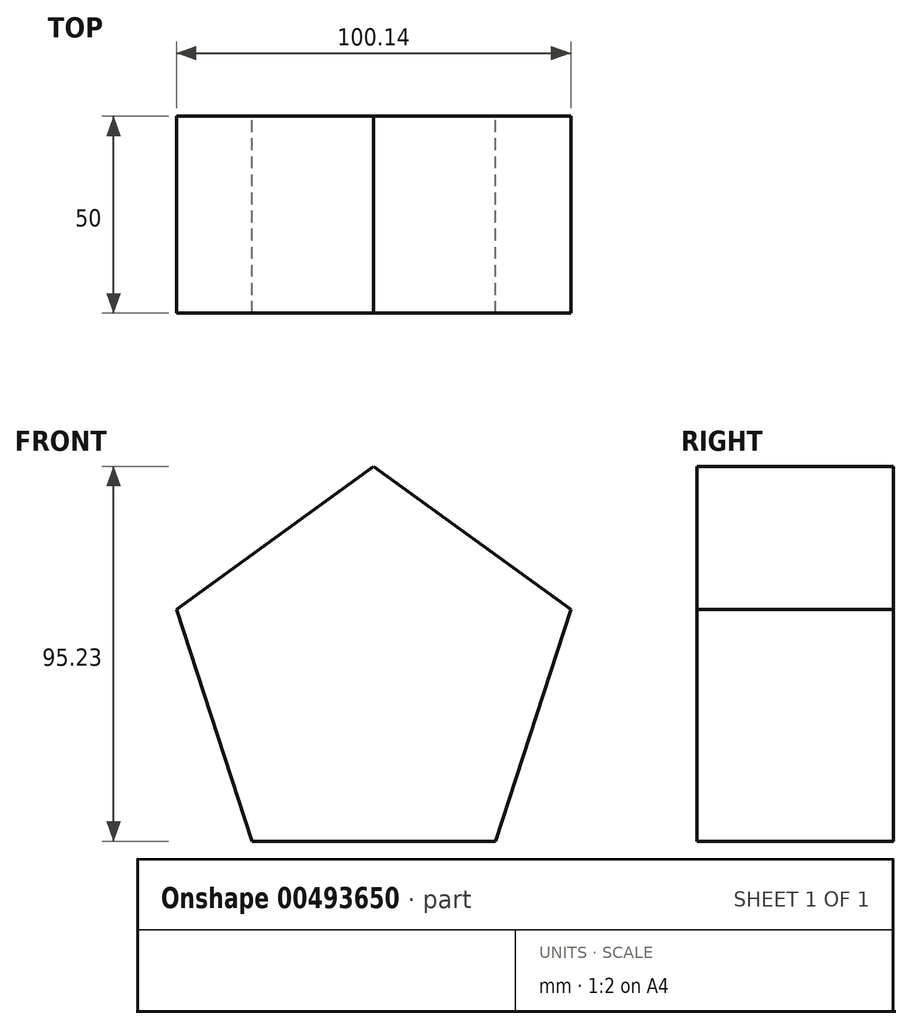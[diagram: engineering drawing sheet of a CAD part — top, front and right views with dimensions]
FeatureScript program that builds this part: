
annotation { "Feature Type Name" : "Feature", "Feature Type Description" : "" }
export const myFeature = defineFeature(function(context is Context, id is Id, definition is map)
    precondition{}
    {
        {
            var Q0;
            Q0=qCreatedBy(makeId("Front.planeOp"),FACE);
            var sketch = newSketch(context, id + "F0", { "sketchPlane" : qUnion([Q0])});
            skCircle(sketch, "E0.cCircle", {"center": v(0, 0) * mm, "radius": 52.64 * mm, "construction": true});
            skLineSegment(sketch, "E0.0", {"start": v(50.07, 16.27) * mm, "end": v(30.94, -42.59) * mm});
            skLineSegment(sketch, "E0.1", {"start": v(30.94, -42.59) * mm, "end": v(-30.94, -42.59) * mm});
            skLineSegment(sketch, "E0.2", {"start": v(-30.94, -42.59) * mm, "end": v(-50.07, 16.27) * mm});
            skLineSegment(sketch, "E0.3", {"start": v(-50.07, 16.27) * mm, "end": v(0, 52.64) * mm});
            skLineSegment(sketch, "E0.4", {"start": v(0, 52.64) * mm, "end": v(50.07, 16.27) * mm});
            skSolve(sketch);
        }
        {
            var Q0;
            Q0=makeQuery(id+"F0.imprint","IMPRINT",FACE,{"disambiguationData":[TD([[makeQuery(id+"F0.imprint","IMPRINT",EDGE,{"derivedFrom":sQuery(id+"F0.wireOp",EDGE,"E0.0")}),-1.0]])]});
            extrude(context, id + "F1", {"entities" : qUnion([Q0]), "depth" : 50 * mm});
        }
    });
